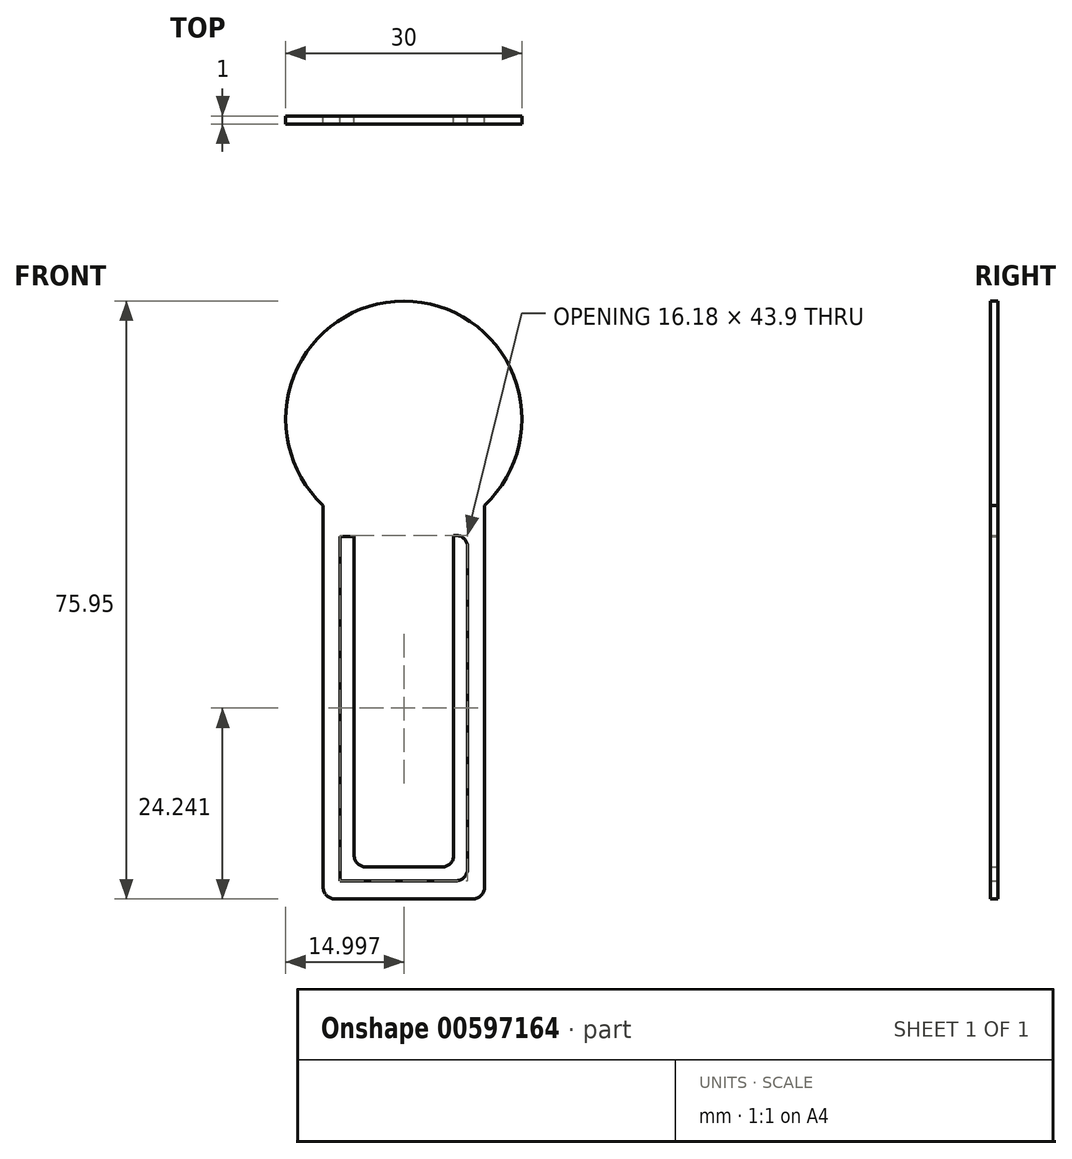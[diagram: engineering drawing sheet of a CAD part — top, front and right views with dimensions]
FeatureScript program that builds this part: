
annotation { "Feature Type Name" : "Feature", "Feature Type Description" : "" }
export const myFeature = defineFeature(function(context is Context, id is Id, definition is map)
    precondition{}
    {
        {
            var Q0;
            Q0=qCreatedBy(makeId("Front.planeOp"),FACE);
            var sketch = newSketch(context, id + "F0", { "sketchPlane" : qUnion([Q0])});
            skCircle(sketch, "E0", {"center": v(-22.83, 37.78) * mm, "radius": 15 * mm});
            skLineSegment(sketch, "E1.bottom", {"start": v(-33.08, 26.83) * mm, "end": v(-12.58, 26.83) * mm});
            skLineSegment(sketch, "E1.top", {"start": v(-33.08, -23.17) * mm, "end": v(-12.58, -23.17) * mm});
            skLineSegment(sketch, "E1.left", {"start": v(-33.08, 26.83) * mm, "end": v(-33.08, -23.17) * mm});
            skLineSegment(sketch, "E1.right", {"start": v(-12.58, 26.83) * mm, "end": v(-12.58, -23.17) * mm});
            skLineSegment(sketch, "E2.bottom", {"start": v(-66.52, 27.4) * mm, "end": v(-68.85, 27.4) * mm});
            skLineSegment(sketch, "E2.top", {"start": v(-66.52, 22.8) * mm, "end": v(-68.85, 22.8) * mm});
            skLineSegment(sketch, "E2.left", {"start": v(-68.85, 22.8) * mm, "end": v(-68.85, 27.4) * mm});
            skLineSegment(sketch, "E2.right", {"start": v(-66.52, 22.8) * mm, "end": v(-66.52, 27.4) * mm});
            skLineSegment(sketch, "E3.bottom", {"start": v(-66.52, 22.8) * mm, "end": v(-64.76, 22.8) * mm});
            skLineSegment(sketch, "E3.top", {"start": v(-66.52, 21.56) * mm, "end": v(-64.76, 21.56) * mm});
            skLineSegment(sketch, "E3.left", {"start": v(-66.52, 22.8) * mm, "end": v(-66.52, 21.56) * mm});
            skLineSegment(sketch, "E3.right", {"start": v(-64.76, 22.8) * mm, "end": v(-64.76, 21.56) * mm});
            skLineSegment(sketch, "E4.bottom", {"start": v(-30.92, 22.88) * mm, "end": v(-29.15, 22.88) * mm});
            skLineSegment(sketch, "E4.top", {"start": v(-30.92, -20.88) * mm, "end": v(-29.15, -20.88) * mm});
            skLineSegment(sketch, "E4.left", {"start": v(-30.92, 22.88) * mm, "end": v(-30.92, -20.88) * mm});
            skLineSegment(sketch, "E4.right", {"start": v(-29.15, 22.88) * mm, "end": v(-29.15, -20.88) * mm});
            skLineSegment(sketch, "E5.bottom", {"start": v(-30.92, -20.88) * mm, "end": v(-14.74, -20.88) * mm});
            skLineSegment(sketch, "E5.top", {"start": v(-30.92, -19.13) * mm, "end": v(-14.74, -19.13) * mm});
            skLineSegment(sketch, "E5.left", {"start": v(-30.92, -20.88) * mm, "end": v(-30.92, -19.13) * mm});
            skLineSegment(sketch, "E5.right", {"start": v(-14.74, -20.88) * mm, "end": v(-14.74, -19.13) * mm});
            skLineSegment(sketch, "E6.bottom", {"start": v(-14.74, -20.88) * mm, "end": v(-16.5, -20.88) * mm});
            skLineSegment(sketch, "E6.top", {"start": v(-14.74, 23.02) * mm, "end": v(-16.5, 23.02) * mm});
            skLineSegment(sketch, "E6.left", {"start": v(-14.74, -20.88) * mm, "end": v(-14.74, 23.02) * mm});
            skLineSegment(sketch, "E6.right", {"start": v(-16.5, -20.88) * mm, "end": v(-16.5, 23.02) * mm});
            skSolve(sketch);
        }
        {
            var Q0;
            {var subQ0=sQuery(id+"F0.wireOp",EDGE,"E1.bottom");var subQ1=sQuery(id+"F0.wireOp",EDGE,"E0");var subQ3=makeQuery(id+"F0.imprint","INTERSECT",VERTEX,{"derivedFrom":[subQ1,subQ0]});Q0=makeQuery(id+"F0.imprint","IMPRINT",FACE,{"disambiguationData":[TD([[makeQuery(id+"F0.imprint","IMPRINT",EDGE,{"disambiguationData":[TD([[subQ3,-1.0]])],"derivedFrom":subQ1}),1.0]])]});}
            var Q1;
            {var subQ0=sQuery(id+"F0.wireOp",EDGE,"E1.bottom");var subQ1=sQuery(id+"F0.wireOp",EDGE,"E0");var subQ3=makeQuery(id+"F0.imprint","INTERSECT",VERTEX,{"derivedFrom":[subQ1,subQ0]});Q1=makeQuery(id+"F0.imprint","IMPRINT",FACE,{"disambiguationData":[TD([[makeQuery(id+"F0.imprint","IMPRINT",EDGE,{"disambiguationData":[TD([[subQ3,1.0]])],"derivedFrom":subQ1}),1.0]])]});}
            var Q2;
            Q2=makeQuery(id+"F0.imprint","IMPRINT",FACE,{"disambiguationData":[TD([[makeQuery(id+"F0.imprint","IMPRINT",EDGE,{"derivedFrom":sQuery(id+"F0.wireOp",EDGE,"E1.top")}),1.0]])]});
            extrude(context, id + "F1", {"entities" : qUnion([Q0, Q1, Q2]), "depth" : 1 * mm, "offsetDistance" : 25 * mm});
        }
        {
            var Q0;
            Q0=makeQuery(id+"F1.opExtrude","SWEPT_EDGE",EDGE,{"disambiguationData":[OSD([sQuery(id+"F0.wireOp",EDGE,"E1.top"),sQuery(id+"F0.wireOp",EDGE,"E1.left")])]});
            var Q1;
            Q1=makeQuery(id+"F1.opExtrude","SWEPT_EDGE",EDGE,{"disambiguationData":[OSD([sQuery(id+"F0.wireOp",EDGE,"E4.right"),sQuery(id+"F0.wireOp",EDGE,"E5.top")])]});
            fillet(context, id + "F2", {"entities" : qUnion([Q0, Q1]), "radius" : 1.5 * mm, "tangentPropagation" : true, "allowEdgeOverflow" : false});
        }
        {
            var Q0;
            Q0=makeQuery(id+"F1.opExtrude","SWEPT_EDGE",EDGE,{"disambiguationData":[OSD([sQuery(id+"F0.wireOp",EDGE,"E1.top"),sQuery(id+"F0.wireOp",EDGE,"E1.right")])]});
            var Q1;
            Q1=makeQuery(id+"F1.opExtrude","SWEPT_EDGE",EDGE,{"disambiguationData":[OSD([sQuery(id+"F0.wireOp",EDGE,"E5.top"),sQuery(id+"F0.wireOp",EDGE,"E6.right")])]});
            fillet(context, id + "F3", {"entities" : qUnion([Q0, Q1]), "radius" : 1.5 * mm, "tangentPropagation" : true, "allowEdgeOverflow" : false});
        }
        {
            var Q0;
            Q0=makeQuery(id+"F1.opExtrude","SWEPT_EDGE",EDGE,{"disambiguationData":[OSD([sQuery(id+"F0.wireOp",EDGE,"E6.bottom"),sQuery(id+"F0.wireOp",EDGE,"E6.left")])]});
            fillet(context, id + "F4", {"entities" : qUnion([Q0]), "radius" : 1.5 * mm, "tangentPropagation" : true, "allowEdgeOverflow" : false});
        }
        {
            var Q0;
            Q0=makeQuery(id+"F1.opExtrude","SWEPT_EDGE",EDGE,{"disambiguationData":[OSD([sQuery(id+"F0.wireOp",EDGE,"E5.bottom"),sQuery(id+"F0.wireOp",EDGE,"E5.left")])]});
            fillet(context, id + "F5", {"entities" : qUnion([Q0]), "radius" : 1.5 * mm, "tangentPropagation" : true, "allowEdgeOverflow" : false});
        }
    });
